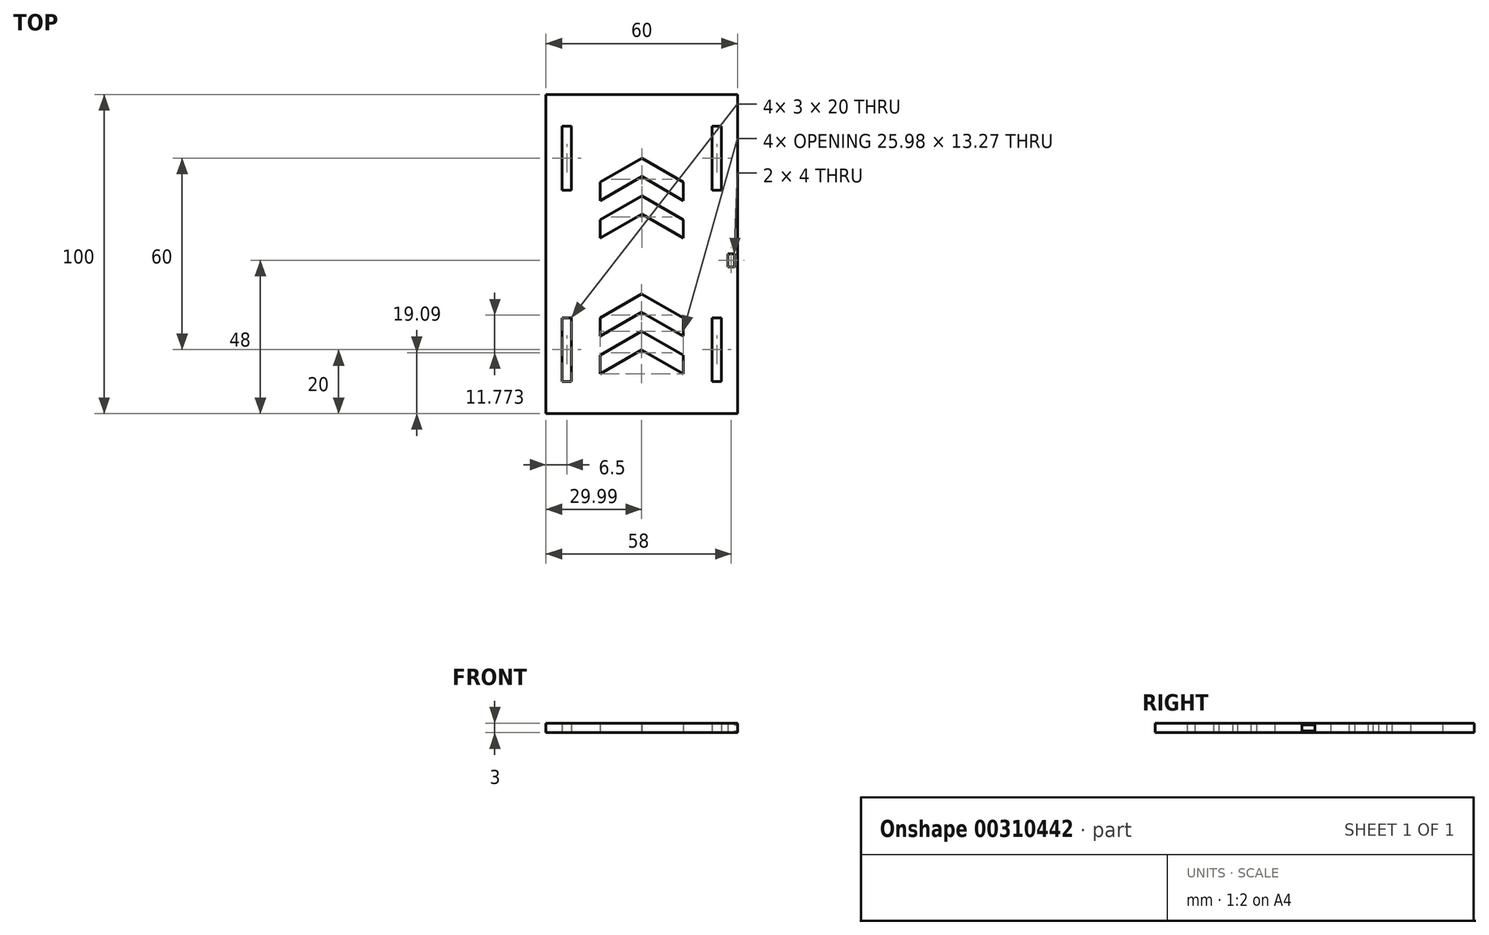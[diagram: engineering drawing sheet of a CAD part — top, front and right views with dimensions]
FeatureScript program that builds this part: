
annotation { "Feature Type Name" : "Feature", "Feature Type Description" : "" }
export const myFeature = defineFeature(function(context is Context, id is Id, definition is map)
    precondition{}
    {
        {
            var Q0;
            Q0=qCreatedBy(makeId("Top.planeOp"),FACE);
            var sketch = newSketch(context, id + "F0", { "sketchPlane" : qUnion([Q0])});
            skLineSegment(sketch, "E0", {"start": v(-30, 0) * mm, "end": v(-30, -100) * mm});
            skLineSegment(sketch, "E1", {"start": v(-30, -100) * mm, "end": v(30, -100) * mm});
            skLineSegment(sketch, "E2", {"start": v(30, -100) * mm, "end": v(30, 0) * mm});
            skLineSegment(sketch, "E3", {"start": v(30, 0) * mm, "end": v(0, 0) * mm});
            skLineSegment(sketch, "E4", {"start": v(-30, 0) * mm, "end": v(0, 0) * mm});
            skLineSegment(sketch, "E5", {"start": v(0, 0) * mm, "end": v(0, -20) * mm});
            skLineSegment(sketch, "E6", {"start": v(0, -20) * mm, "end": v(-13, -27.5) * mm});
            skLineSegment(sketch, "E7", {"start": v(0, -20) * mm, "end": v(13, -27.5) * mm});
            skLineSegment(sketch, "E8", {"start": v(0, -25.77) * mm, "end": v(-13, -33.27) * mm});
            skLineSegment(sketch, "E9", {"start": v(-13, -33.27) * mm, "end": v(-13, -27.5) * mm});
            skLineSegment(sketch, "E10", {"start": v(0, -25.77) * mm, "end": v(13, -33.27) * mm});
            skLineSegment(sketch, "E11", {"start": v(13, -27.5) * mm, "end": v(13, -33.27) * mm});
            skLineSegment(sketch, "E12", {"start": v(0, -31.77) * mm, "end": v(-13, -39.27) * mm});
            skLineSegment(sketch, "E13", {"start": v(0, -31.77) * mm, "end": v(13, -39.27) * mm});
            skLineSegment(sketch, "E14", {"start": v(0, -37.55) * mm, "end": v(-13, -45.05) * mm});
            skLineSegment(sketch, "E15", {"start": v(-13, -45.05) * mm, "end": v(-13, -39.27) * mm});
            skLineSegment(sketch, "E16", {"start": v(0, -37.55) * mm, "end": v(13, -45.05) * mm});
            skLineSegment(sketch, "E17", {"start": v(13, -39.27) * mm, "end": v(13, -45.05) * mm});
            skLineSegment(sketch, "E18", {"start": v(0, -100) * mm, "end": v(0, -80) * mm});
            skPoint(sketch, "E18.endSnap0", {"position": v(0, -100) * mm});
            skLineSegment(sketch, "E19.1.0.0", {"start": v(0, -62.5) * mm, "end": v(-13, -70) * mm});
            skLineSegment(sketch, "E19.1.0.1", {"start": v(-13, -87.55) * mm, "end": v(-13, -81.77) * mm});
            skLineSegment(sketch, "E19.1.0.2", {"start": v(12.98, -70) * mm, "end": v(12.98, -75.77) * mm});
            skLineSegment(sketch, "E19.1.0.4", {"start": v(0, -68.27) * mm, "end": v(12.98, -75.77) * mm});
            skLineSegment(sketch, "E19.1.0.5", {"start": v(-13, -75.77) * mm, "end": v(-13, -70) * mm});
            skLineSegment(sketch, "E19.1.0.6", {"start": v(0, -68.27) * mm, "end": v(-13, -75.77) * mm});
            skLineSegment(sketch, "E19.1.0.7", {"start": v(12.98, -81.77) * mm, "end": v(12.98, -87.55) * mm});
            skLineSegment(sketch, "E19.1.0.8", {"start": v(0, -62.5) * mm, "end": v(12.98, -70) * mm});
            skLineSegment(sketch, "E19.1.0.9", {"start": v(0, -80.05) * mm, "end": v(-13, -87.55) * mm});
            skLineSegment(sketch, "E19.1.0.10", {"start": v(0, -74.27) * mm, "end": v(12.98, -81.77) * mm});
            skLineSegment(sketch, "E19.1.0.11", {"start": v(0, -80.05) * mm, "end": v(12.98, -87.55) * mm});
            skLineSegment(sketch, "E19.1.0.12", {"start": v(0, -74.27) * mm, "end": v(-13, -81.77) * mm});
            skLineSegment(sketch, "E19.direction1", {"start": v(-13, -27.5) * mm, "end": v(-13, -70) * mm, "construction": true});
            skLineSegment(sketch, "E20", {"start": v(-30, 0) * mm, "end": v(-25, 0) * mm});
            skLineSegment(sketch, "E21", {"start": v(-25, 0) * mm, "end": v(-25, -10) * mm});
            skLineSegment(sketch, "E22", {"start": v(-25, -10) * mm, "end": v(-25, -30) * mm});
            skLineSegment(sketch, "E23", {"start": v(-25, -10) * mm, "end": v(-22, -10) * mm});
            skLineSegment(sketch, "E24", {"start": v(-22, -10) * mm, "end": v(-22, -30) * mm});
            skLineSegment(sketch, "E25", {"start": v(-22, -30) * mm, "end": v(-25, -30) * mm});
            skLineSegment(sketch, "E26", {"start": v(-25, -70) * mm, "end": v(-25, -90) * mm});
            skLineSegment(sketch, "E27", {"start": v(-22, -90) * mm, "end": v(-25, -90) * mm});
            skLineSegment(sketch, "E28", {"start": v(-25, -70) * mm, "end": v(-22, -70) * mm});
            skLineSegment(sketch, "E29", {"start": v(-22, -70) * mm, "end": v(-22, -90) * mm});
            skLineSegment(sketch, "E30.MirrorCS", {"start": v(22, -30) * mm, "end": v(25, -30) * mm});
            skLineSegment(sketch, "E31.MirrorCS", {"start": v(25, -70) * mm, "end": v(22, -70) * mm});
            skLineSegment(sketch, "E32.MirrorCS", {"start": v(25, -10) * mm, "end": v(22, -10) * mm});
            skLineSegment(sketch, "E33.MirrorCS", {"start": v(22, -90) * mm, "end": v(25, -90) * mm});
            skLineSegment(sketch, "E34.MirrorCS", {"start": v(25, -10) * mm, "end": v(25, -30) * mm});
            skLineSegment(sketch, "E35.MirrorCS", {"start": v(22, -70) * mm, "end": v(22, -90) * mm});
            skLineSegment(sketch, "E36.MirrorCS", {"start": v(25, -70) * mm, "end": v(25, -90) * mm});
            skLineSegment(sketch, "E37.MirrorCS", {"start": v(22, -10) * mm, "end": v(22, -30) * mm});
            skLineSegment(sketch, "E38", {"start": v(0, 0) * mm, "end": v(-30, -50) * mm});
            skLineSegment(sketch, "E39", {"start": v(0, 0) * mm, "end": v(0, -50) * mm});
            skLineSegment(sketch, "E40", {"start": v(30, -50) * mm, "end": v(29, -50) * mm});
            skPoint(sketch, "E40.endSnap0", {"position": v(30, -50) * mm});
            skLineSegment(sketch, "E41", {"start": v(29, -50) * mm, "end": v(29, -54) * mm});
            skLineSegment(sketch, "E42", {"start": v(29, -54) * mm, "end": v(27, -54) * mm});
            skLineSegment(sketch, "E43", {"start": v(27, -54) * mm, "end": v(27, -50) * mm});
            skLineSegment(sketch, "E44", {"start": v(27, -50) * mm, "end": v(29, -50) * mm});
            skSolve(sketch);
        }
        {
            var Q0;
            Q0 = qSketchRegion(id + "F0", true);
            extrude(context, id + "F1", {"entities" : qUnion([Q0]), "depth" : 3 * mm});
        }
        {
            var Q0;
            Q0=makeQuery(id+"F1.opExtrude","SWEPT_FACE",FACE,{"disambiguationData":[OSD([sQuery(id+"F0.wireOp",EDGE,"E2")])]});
            cPlane(context, id + "F2", {"entities" : qUnion([Q0]), "cplaneType" : CPlaneType.OFFSET, "offset" : 0 * mm, "width" : 150 * mm, "height" : 150 * mm});
        }
        {
            var Q0;
            Q0=qCreatedBy(id+"F2.planeOp",FACE);
            var sketch = newSketch(context, id + "F3", { "sketchPlane" : qUnion([Q0])});
            skLineSegment(sketch, "E45", {"start": v(0, 0) * mm, "end": v(-50, 0) * mm});
            skLineSegment(sketch, "E46", {"start": v(-50, 0) * mm, "end": v(-50, 0.5) * mm});
            skLineSegment(sketch, "E47", {"start": v(0, 0) * mm, "end": v(0, 3) * mm});
            skLineSegment(sketch, "E48", {"start": v(0, 3) * mm, "end": v(-50, 3) * mm});
            skLineSegment(sketch, "E49", {"start": v(-50, 3) * mm, "end": v(-50, 2.5) * mm});
            skLineSegment(sketch, "E50", {"start": v(-50, 2.5) * mm, "end": v(-54, 2.5) * mm});
            skLineSegment(sketch, "E51", {"start": v(-54, 2.5) * mm, "end": v(-54, 0.5) * mm});
            skLineSegment(sketch, "E52", {"start": v(-54, 0.5) * mm, "end": v(-50, 0.5) * mm});
            skLineSegment(sketch, "E53", {"start": v(-50, 2.5) * mm, "end": v(-50, 0.5) * mm});
            skSolve(sketch);
        }
        {
            var Q0;
            Q0=makeQuery(id+"F3.imprint","IMPRINT",FACE,{"disambiguationData":[TD([[makeQuery(id+"F3.imprint","IMPRINT",EDGE,{"derivedFrom":sQuery(id+"F3.wireOp",EDGE,"E50")}),1.0]])]});
            var Q1;
            Q1=makeQuery(id+"F1.opExtrude","SWEPT_FACE",FACE,{"disambiguationData":[OSD([sQuery(id+"F0.wireOp",EDGE,"E43")])]});
            extrude(context, id + "F4", {"entities" : qUnion([Q0]), "operationType" : NewBodyOperationType.REMOVE, "endBound" : BoundingType.UP_TO_SURFACE, "oppositeDirection" : true, "endBoundEntityFace" : qUnion([Q1]), "depth" : 25 * mm});
        }
    });
